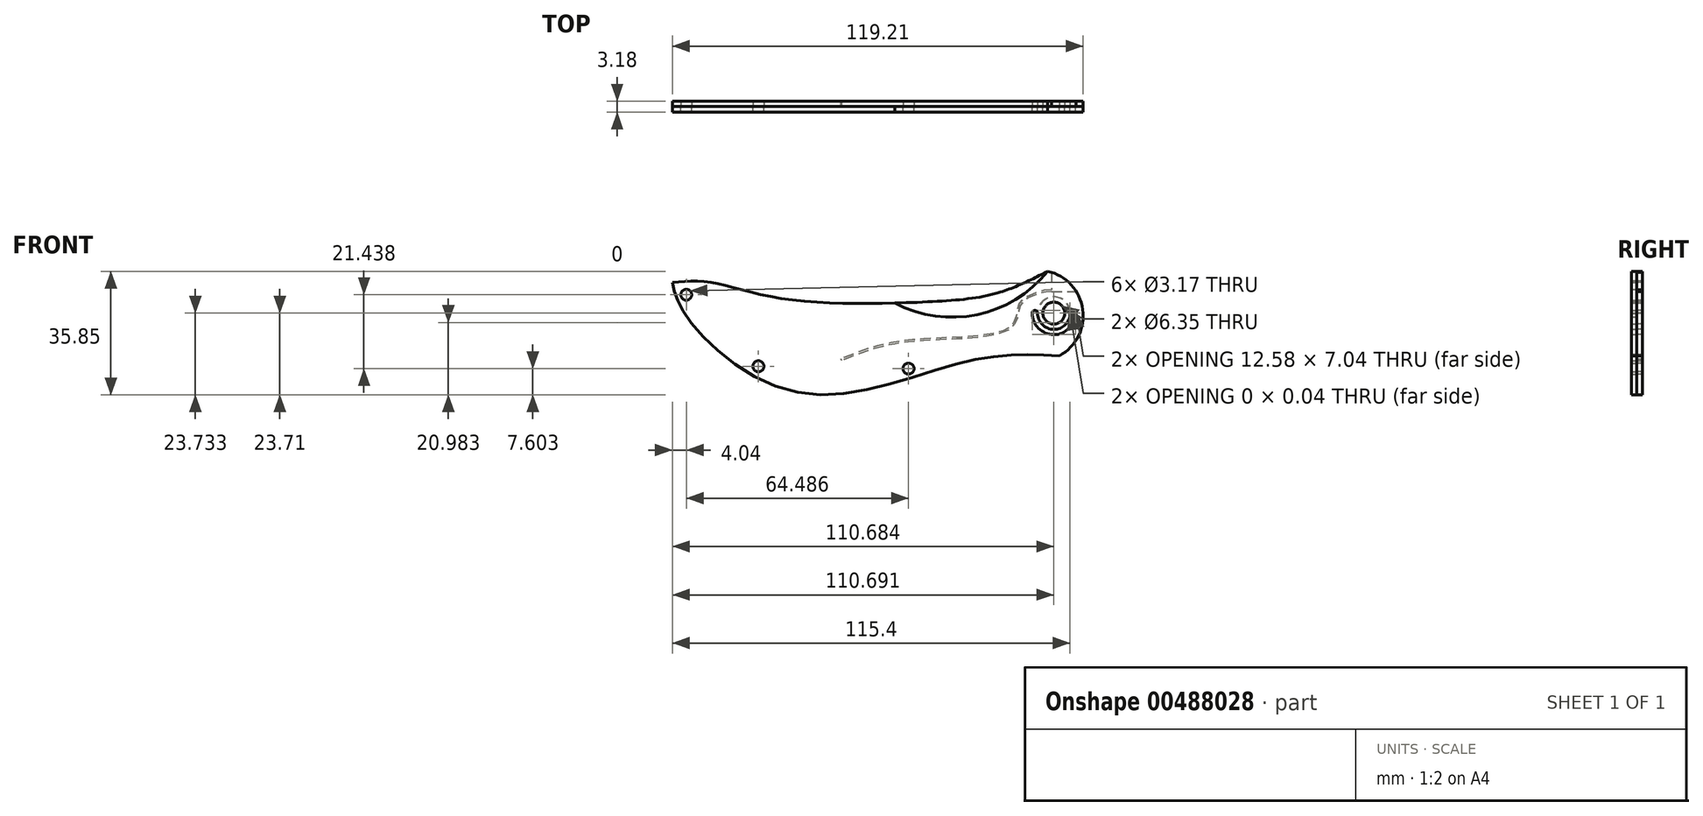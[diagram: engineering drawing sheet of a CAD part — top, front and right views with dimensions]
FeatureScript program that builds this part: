
annotation { "Feature Type Name" : "Feature", "Feature Type Description" : "" }
export const myFeature = defineFeature(function(context is Context, id is Id, definition is map)
    precondition{}
    {
        {
            var Q0;
            Q0=qCreatedBy(makeId("Front.planeOp"),FACE);
            var sketch = newSketch(context, id + "F0", { "sketchPlane" : qUnion([Q0])});
            skArc(sketch, "E0", {"start": v(22.09, -11.71) * mm, "mid": v(28.86, 1.7) * mm, "end": v(18.7, 12.78) * mm});
            skFitSpline(sketch, "E1", {"points": [v(22.09, -11.71) * mm, v(-5.38, -13.48) * mm, v(-53.51, -22.45) * mm, v(-86.35, 0) * mm, v(-90.23, 9.57) * mm], "startDerivative": vector(-105.1, 4.78) * mm, "endDerivative": vector(-12.4, 57.23) * mm});
            skFitSpline(sketch, "E2", {"points": [v(-90.23, 9.57) * mm, v(-79.42, 9.57) * mm, v(-58.61, 4.88) * mm, v(-17.41, 3.86) * mm, v(4.2, 6.51) * mm, v(18.7, 12.78) * mm], "startDerivative": vector(72.07, 6.04) * mm, "endDerivative": vector(81.13, 41.47) * mm});
            skPoint(sketch, "E3", {"position": v(20.46, 0.64) * mm});
            skPoint(sketch, "E4", {"position": v(25.96, 0.67) * mm});
            skPoint(sketch, "E5", {"position": v(14.96, 0.67) * mm});
            skArc(sketch, "E6", {"start": v(14.16, 0.7) * mm, "mid": v(14.16, 0.67) * mm, "end": v(14.16, 0.64) * mm});
            skArc(sketch, "E7", {"start": v(25.17, 0.68) * mm, "mid": v(25.17, 0.66) * mm, "end": v(25.17, 0.64) * mm});
            skCircle(sketch, "E8", {"center": v(20.46, 0.64) * mm, "radius": 3.18 * mm});
            skArc(sketch, "E9", {"start": v(25.17, 0.64) * mm, "mid": v(15.75, 0.66) * mm, "end": v(25.17, 0.6) * mm});
            skArc(sketch, "E10", {"start": v(18.7, 12.78) * mm, "mid": v(10.76, 11.23) * mm, "end": v(4.2, 6.51) * mm});
            skCircle(sketch, "E11", {"center": v(-86.2, 5.97) * mm, "radius": 1.59 * mm});
            skCircle(sketch, "E12", {"center": v(-65.27, -14.78) * mm, "radius": 1.59 * mm});
            skCircle(sketch, "E13", {"center": v(-21.7, -15.47) * mm, "radius": 1.59 * mm});
            skArc(sketch, "E14.MirrorCS", {"start": v(25.17, 0.6) * mm, "mid": v(20.43, -4.08) * mm, "end": v(15.75, 0.67) * mm});
            skArc(sketch, "E15.MirrorCS", {"start": v(26.74, 0.56) * mm, "mid": v(20.4, -5.6) * mm, "end": v(14.16, 0.68) * mm});
            skArc(sketch, "E16.trimOffspring", {"start": v(15.75, 0.64) * mm, "mid": v(15.75, 0.66) * mm, "end": v(15.75, 0.68) * mm});
            skArc(sketch, "E17", {"start": v(15.75, 0.67) * mm, "mid": v(14.97, 1.43) * mm, "end": v(14.16, 0.7) * mm});
            skArc(sketch, "E18", {"start": v(26.74, 0.56) * mm, "mid": v(25.97, 1.38) * mm, "end": v(25.17, 0.6) * mm});
            skArc(sketch, "E19.trimOffspring", {"start": v(15.75, 0.67) * mm, "mid": v(15.75, 0.65) * mm, "end": v(15.75, 0.64) * mm});
            skPoint(sketch, "E20.start.orphan", {"position": v(26.76, 0.64) * mm});
            skSolve(sketch);
        }
        {
            var Q0;
            Q0=makeQuery(id+"F0.imprint","IMPRINT",FACE,{"disambiguationData":[TD([[makeQuery(id+"F0.imprint","IMPRINT",EDGE,{"derivedFrom":sQuery(id+"F0.wireOp",EDGE,"E0")}),1.0]])]});
            extrude(context, id + "F1", {"entities" : qUnion([Q0]), "depth" : 1.59 * mm});
        }
        {
            var Q0;
            Q0=makeQuery(id+"F1.opExtrude","SWEPT_BODY",BODY,{"disambiguationData":[OSD([sQuery(id+"F0.wireOp",EDGE,"E0"),sQuery(id+"F0.wireOp",EDGE,"E1"),sQuery(id+"F0.wireOp",EDGE,"E2"),sQuery(id+"F0.wireOp",EDGE,"E6"),sQuery(id+"F0.wireOp",EDGE,"E7"),sQuery(id+"F0.wireOp",EDGE,"E8"),sQuery(id+"F0.wireOp",EDGE,"E9"),sQuery(id+"F0.wireOp",EDGE,"E20")])]});
            var Q1;
            Q1=qCreatedBy(makeId("Front.planeOp"),FACE);
            mirror(context, id + "F2", {"entities" : qUnion([Q0]), "mirrorPlane" : qUnion([Q1])});
        }
        {
            var Q0;
            Q0=makeQuery(id+"F2.opPattern","COPY",FACE,{"derivedFrom":makeQuery(id+"F1.opExtrude","CAP_FACE",FACE,{"disambiguationData":[OSD([sQuery(id+"F0.wireOp",EDGE,"E0"),sQuery(id+"F0.wireOp",EDGE,"E1"),sQuery(id+"F0.wireOp",EDGE,"E2"),sQuery(id+"F0.wireOp",EDGE,"E6"),sQuery(id+"F0.wireOp",EDGE,"E8"),sQuery(id+"F0.wireOp",EDGE,"E9"),sQuery(id+"F0.wireOp",EDGE,"E10"),sQuery(id+"F0.wireOp",EDGE,"E11"),sQuery(id+"F0.wireOp",EDGE,"E12"),sQuery(id+"F0.wireOp",EDGE,"E13"),sQuery(id+"F0.wireOp",EDGE,"E15.MirrorCS"),sQuery(id+"F0.wireOp",EDGE,"E16.trimOffspring"),sQuery(id+"F0.wireOp",EDGE,"E17"),sQuery(id+"F0.wireOp",EDGE,"E18")])],"isStart":false}),"instanceName":"1"});
            var sketch = newSketch(context, id + "F3", { "sketchPlane" : qUnion([Q0])});
            skLineSegment(sketch, "E21.bottom", {"start": v(-19.81, 17.1) * mm, "end": v(-32.51, 17.1) * mm});
            skLineSegment(sketch, "E21.top", {"start": v(-19.81, 6.94) * mm, "end": v(-32.51, 6.94) * mm});
            skLineSegment(sketch, "E21.left", {"start": v(-19.81, 17.1) * mm, "end": v(-19.81, 6.94) * mm});
            skLineSegment(sketch, "E21.right", {"start": v(-32.51, 17.1) * mm, "end": v(-32.51, 6.94) * mm});
            skFitSpline(sketch, "E22", {"points": [v(-19.81, 6.94) * mm, v(-14.4, 5.64) * mm, v(-10.78, 2.94) * mm, v(-8.16, -3.63) * mm, v(21.5, -7.7) * mm, v(41.1, -13.15) * mm], "startDerivative": vector(39.36, 0) * mm, "endDerivative": vector(62.57, -25.67) * mm});
            skFitSpline(sketch, "E23.0", {"points": [v(-19.81, 7.45) * mm, v(-18.94, 7.45) * mm, v(-17.63, 7.25) * mm, v(-15.93, 6.75) * mm, v(-14.9, 6.38) * mm, v(-14.1, 6.07) * mm, v(-13.32, 5.74) * mm, v(-12.38, 5.3) * mm, v(-11.52, 4.71) * mm, v(-10.93, 4.12) * mm, v(-10.55, 3.61) * mm, v(-10.24, 3.02) * mm, v(-10.02, 2.37) * mm, v(-9.85, 1.7) * mm, v(-9.67, 0.78) * mm, v(-9.44, -0.4) * mm, v(-9.08, -1.52) * mm, v(-8.64, -2.33) * mm, v(-8.22, -2.9) * mm, v(-7.67, -3.4) * mm, v(-6.97, -3.87) * mm, v(-6.12, -4.29) * mm, v(-4.8, -4.79) * mm, v(-2.85, -5.3) * mm, v(-0.1, -5.74) * mm, v(3.96, -6.17) * mm, v(8.47, -6.4) * mm, v(13.07, -6.6) * mm, v(16.5, -6.78) * mm, v(19.24, -6.96) * mm, v(21.34, -7.16) * mm, v(23.36, -7.4) * mm, v(25.73, -7.76) * mm, v(29.24, -8.46) * mm, v(33.17, -9.55) * mm, v(37.37, -11.07) * mm, v(39.99, -12.14) * mm, v(41.3, -12.68) * mm]});
            skLineSegment(sketch, "E24", {"start": v(41.1, -13.15) * mm, "end": v(41.3, -12.68) * mm});
            skSolve(sketch);
        }
        {
            var Q0;
            Q0 = qSketchRegion(id + "F3", true);
            extrude(context, id + "F4", {"entities" : qUnion([Q0]), "operationType" : NewBodyOperationType.REMOVE, "oppositeDirection" : true, "depth" : 1.59 * mm});
        }
        {
            var Q0;
            Q0=makeQuery(id+"F1.opExtrude","CAP_FACE",FACE,{"disambiguationData":[OSD([sQuery(id+"F0.wireOp",EDGE,"E0"),sQuery(id+"F0.wireOp",EDGE,"E1"),sQuery(id+"F0.wireOp",EDGE,"E2"),sQuery(id+"F0.wireOp",EDGE,"E6"),sQuery(id+"F0.wireOp",EDGE,"E8"),sQuery(id+"F0.wireOp",EDGE,"E9"),sQuery(id+"F0.wireOp",EDGE,"E10"),sQuery(id+"F0.wireOp",EDGE,"E11"),sQuery(id+"F0.wireOp",EDGE,"E12"),sQuery(id+"F0.wireOp",EDGE,"E13"),sQuery(id+"F0.wireOp",EDGE,"E15.MirrorCS"),sQuery(id+"F0.wireOp",EDGE,"E16.trimOffspring"),sQuery(id+"F0.wireOp",EDGE,"E17"),sQuery(id+"F0.wireOp",EDGE,"E18")])],"isStart":false});
            var sketch = newSketch(context, id + "F5", { "sketchPlane" : qUnion([Q0])});
            skArc(sketch, "E25", {"start": v(-25.74, 3.56) * mm, "mid": v(-1.87, 0.19) * mm, "end": v(18.7, 12.78) * mm});
            skFitSpline(sketch, "E26", {"points": [v(18.7, 12.78) * mm, v(-25.74, 3.56) * mm], "startDerivative": vector(-47.02, 15.59) * mm, "endDerivative": vector(-44.43, -9.22) * mm});
            skSolve(sketch);
        }
        {
            var Q0;
            {var subQ0=sQuery(id+"F5.wireOp",EDGE,"E26");Q0=makeQuery(id+"F5.imprint","IMPRINT",FACE,{"disambiguationData":[TD([[makeQuery(id+"F5.imprint","IMPRINT",EDGE,{"derivedFrom":subQ0}),1.0]])]});}
            extrude(context, id + "F6", {"entities" : qUnion([Q0]), "operationType" : NewBodyOperationType.REMOVE, "oppositeDirection" : true, "depth" : 1.59 * mm});
        }
        {
            var Q0;
            Q0 = qSketchRegion(id + "F5", true);
            extrude(context, id + "F7", {"entities" : qUnion([Q0]), "operationType" : NewBodyOperationType.REMOVE, "oppositeDirection" : true, "depth" : 1.59 * mm});
        }
    });
